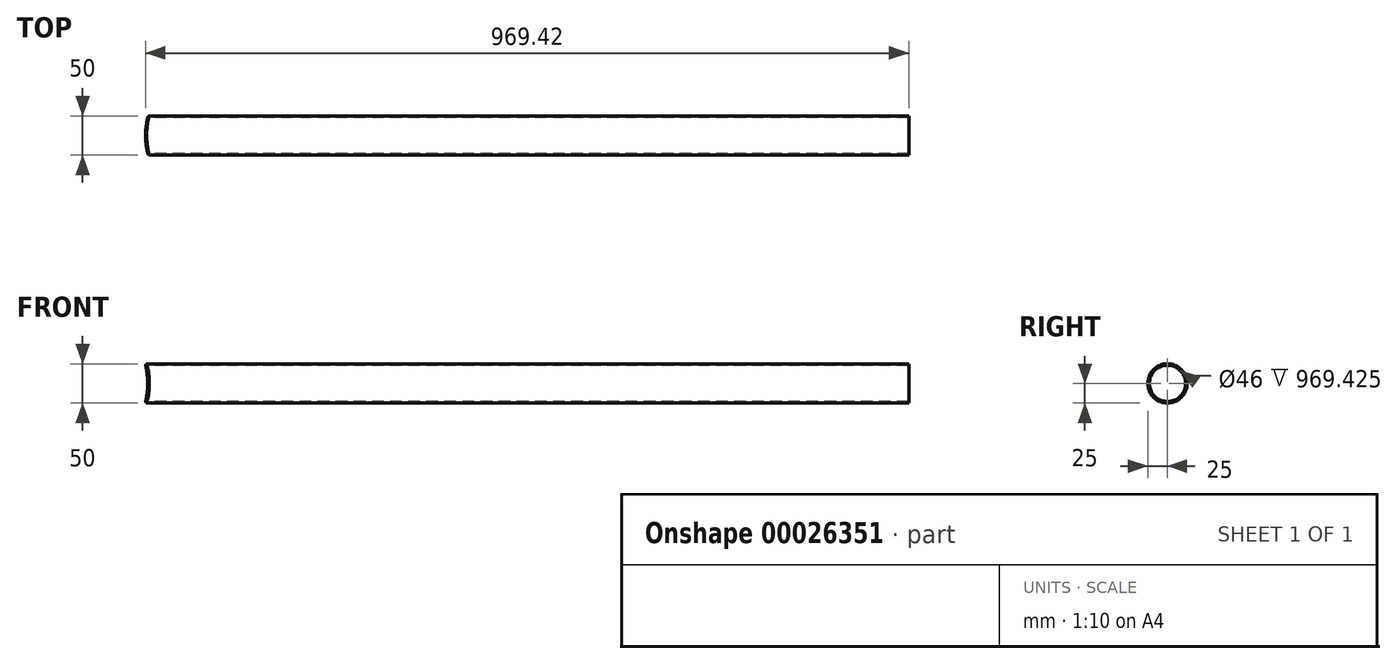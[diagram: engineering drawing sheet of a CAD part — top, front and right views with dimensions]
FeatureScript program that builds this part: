
annotation { "Feature Type Name" : "Feature", "Feature Type Description" : "" }
export const myFeature = defineFeature(function(context is Context, id is Id, definition is map)
    precondition{}
    {
        {
            var Q0;
            Q0=qCreatedBy(makeId("Right.planeOp"),FACE);
            var sketch = newSketch(context, id + "F0", { "sketchPlane" : qUnion([Q0])});
            skCircle(sketch, "E0", {"center": v(0, 0) * mm, "radius": 25 * mm});
            skCircle(sketch, "E1", {"center": v(0, 0) * mm, "radius": 23 * mm});
            skSolve(sketch);
        }
        {
            var Q0;
            Q0=makeQuery(id+"F0.imprint","IMPRINT",FACE,{"disambiguationData":[TD([[makeQuery(id+"F0.imprint","IMPRINT",EDGE,{"derivedFrom":sQuery(id+"F0.wireOp",EDGE,"E0")}),1.0]])]});
            extrude(context, id + "F1", {"entities" : qUnion([Q0]), "depth" : 1000 * mm});
        }
        {
            var Q0;
            Q0=qCreatedBy(makeId("Front.planeOp"),FACE);
            var sketch = newSketch(context, id + "F2", { "sketchPlane" : qUnion([Q0])});
            skCircle(sketch, "E2", {"center": v(0, 0) * mm, "radius": 25 * mm});
            skCircle(sketch, "E3", {"center": v(0, 0) * mm, "radius": 23 * mm});
            skSolve(sketch);
        }
        {
            var Q0;
            Q0 = qSketchRegion(id + "F2", true);
            extrude(context, id + "F3", {"entities" : qUnion([Q0]), "endBound" : BoundingType.SYMMETRIC, "depth" : 500 * mm});
        }
        {
            var Q0;
            Q0=qCreatedBy(makeId("Front.planeOp"),FACE);
            var sketch = newSketch(context, id + "F4", { "sketchPlane" : qUnion([Q0])});
            skCircle(sketch, "E4.0", {"center": v(0, 0) * mm, "radius": 25.2 * mm});
            skSolve(sketch);
        }
        {
            var Q0;
            Q0=makeQuery(id+"F4.imprint","IMPRINT",FACE,{"disambiguationData":[TD([[makeQuery(id+"F4.imprint","IMPRINT",EDGE,{"derivedFrom":sQuery(id+"F4.wireOp",EDGE,"E4.0")}),1.0]])]});
            var Q1;
            Q1=makeQuery(id+"F1.opExtrude","SWEPT_FACE",FACE,{"disambiguationData":[OSD([sQuery(id+"F0.wireOp",EDGE,"E0")])]});
            extrude(context, id + "F5", {"entities" : qUnion([Q0]), "operationType" : NewBodyOperationType.REMOVE, "endBound" : BoundingType.THROUGH_ALL, "oppositeDirection" : true, "endBoundEntityFace" : qUnion([Q1]), "depth" : 25 * mm, "hasSecondDirection" : true, "secondDirectionBound" : SecondDirectionBoundingType.THROUGH_ALL, "secondDirectionOppositeDirection" : false, "secondDirectionDepth" : 25 * mm});
        }
        {
            var Q0;
            Q0=makeQuery(id+"F5.boolean.opBoolean","INTERSECT",EDGE,{"derivedFrom":[makeQuery(id+"F1.opExtrude","SWEPT_FACE",FACE,{"disambiguationData":[OSD([sQuery(id+"F0.wireOp",EDGE,"E0")])]}),makeQuery(id+"F5.opExtrude","SWEPT_FACE",FACE,{"disambiguationData":[OSD([sQuery(id+"F4.wireOp",EDGE,"E4.0")])]})]});
            chamfer(context, id + "F6", {"entities" : qUnion([Q0]), "width" : 10 * mm, "tangentPropagation" : true});
        }
    });
